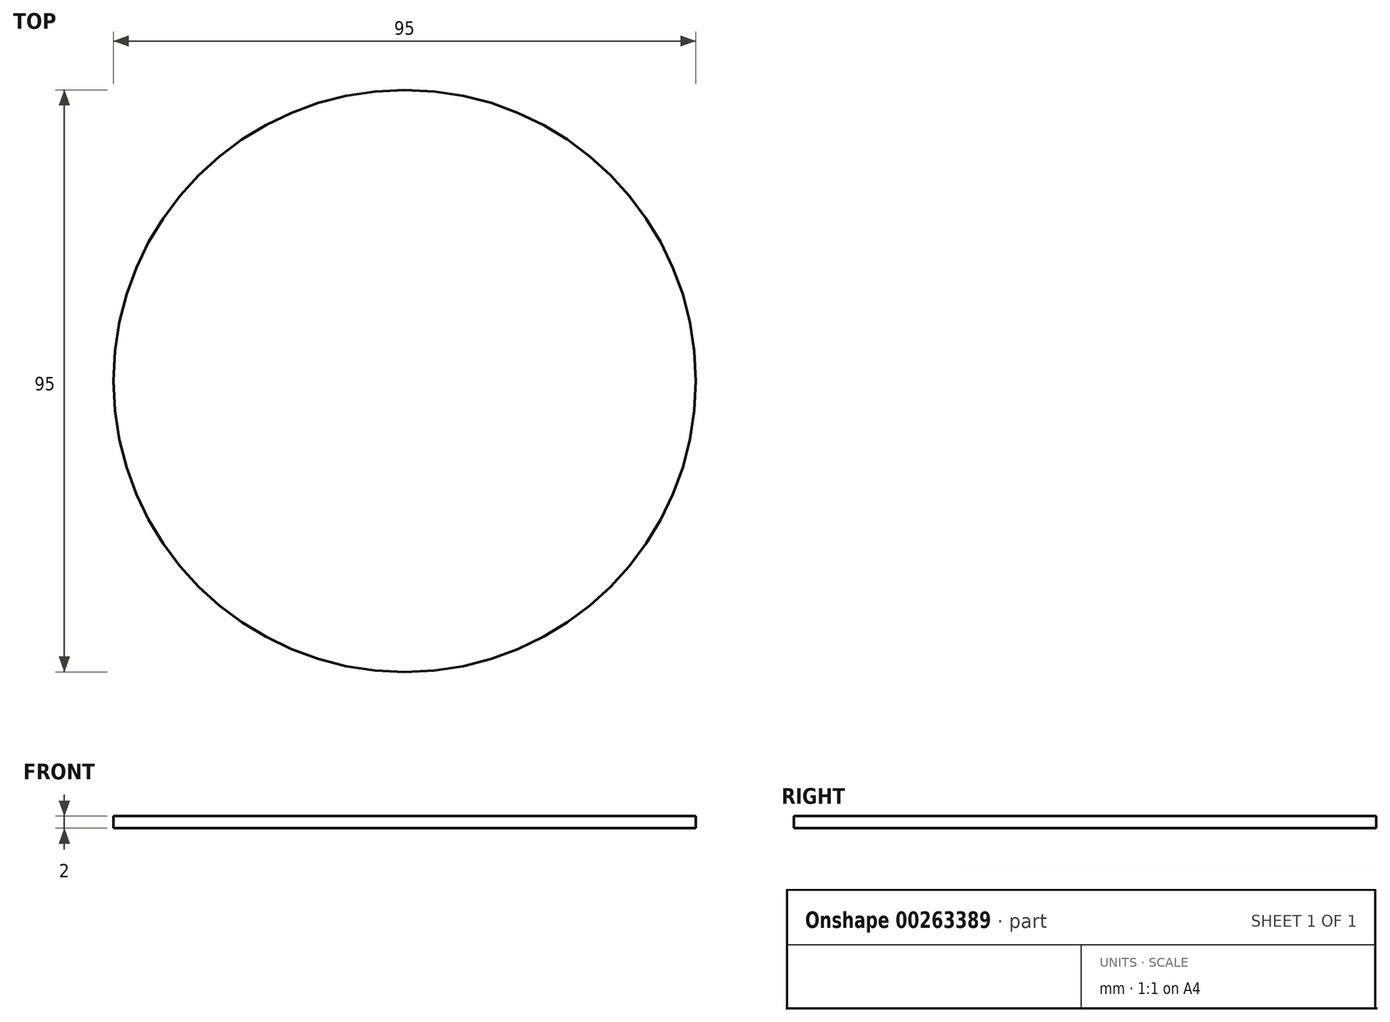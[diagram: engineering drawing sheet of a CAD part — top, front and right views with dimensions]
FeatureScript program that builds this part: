
annotation { "Feature Type Name" : "Feature", "Feature Type Description" : "" }
export const myFeature = defineFeature(function(context is Context, id is Id, definition is map)
    precondition{}
    {
        {
            var Q0;
            Q0=qCreatedBy(makeId("Top.planeOp"),FACE);
            var sketch = newSketch(context, id + "F0", { "sketchPlane" : qUnion([Q0])});
            skCircle(sketch, "E0", {"center": v(0, 0) * mm, "radius": 47.5 * mm});
            skSolve(sketch);
        }
        {
            var Q0;
            Q0=makeQuery(id+"F0.imprint","IMPRINT",FACE,{"disambiguationData":[TD([[makeQuery(id+"F0.imprint","IMPRINT",EDGE,{"derivedFrom":sQuery(id+"F0.wireOp",EDGE,"E0")}),1.0]])]});
            extrude(context, id + "F1", {"entities" : qUnion([Q0]), "depth" : 2 * mm});
        }
    });
